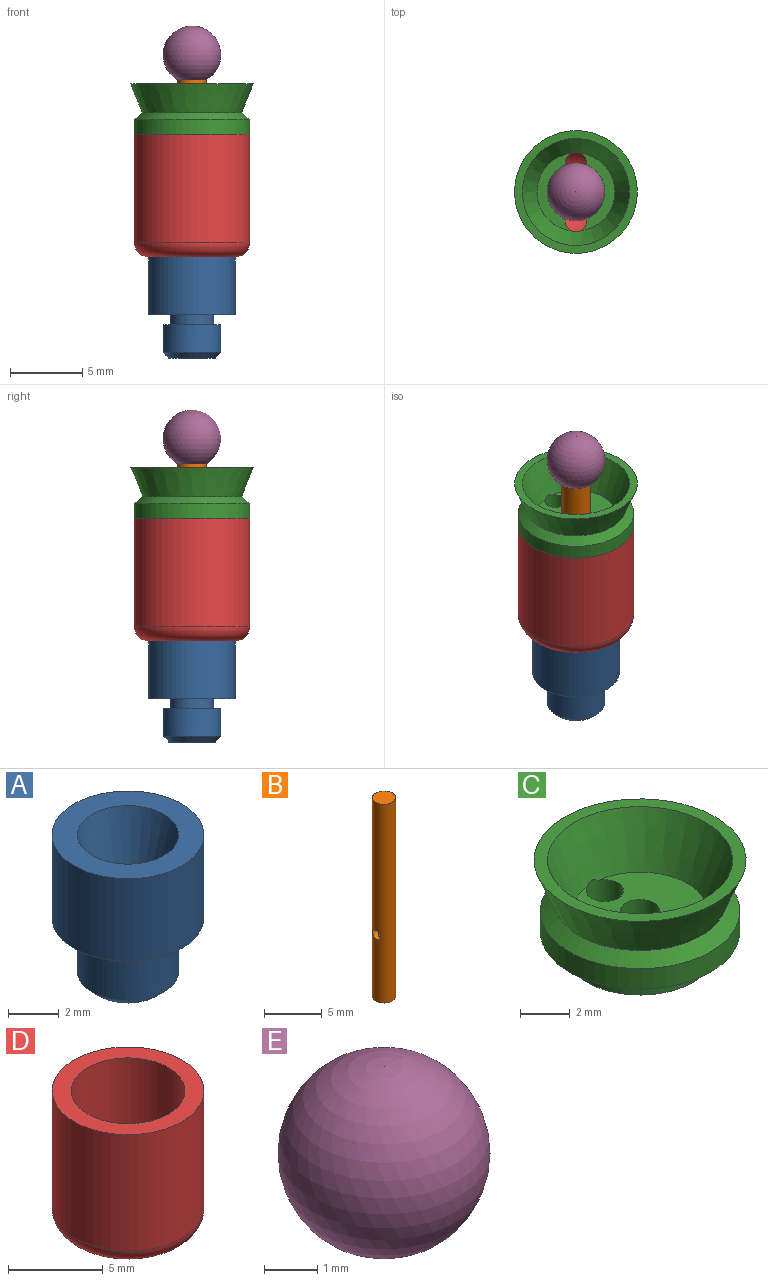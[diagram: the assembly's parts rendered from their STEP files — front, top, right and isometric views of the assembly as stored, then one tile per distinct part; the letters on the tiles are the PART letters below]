
ASSEMBLY  parts=5 mates=4
PART A: 11 faces, bbox 6x6x7 mm
  f0: plane 2x2mm, normal (0,0,1), area 1.1mm2, adj f8,f10
  f1: plane 3.2x3.2mm, normal (0,0,-1), area 6mm2, adj f9,f10
  f2: cylinder r=2mm len=4mm, axis (0,0,-1), area 23.9mm2, adj f3,f9
  f3: plane 4x4mm, normal (0,0,1), area 5.5mm2, adj f2,f4
  f4: cylinder r=1.5mm len=3mm, axis (0,0,-1), area 6.6mm2, adj f3,f5
  f5: plane 6x6mm, normal (0,0,-1), area 21.2mm2, adj f4,f6
  f6: cylinder r=3mm len=6mm, axis (0,0,-1), area 75.4mm2, adj f5,f7
  f7: plane 6x6mm, normal (0,0,1), area 15.7mm2, adj f6,f8
  f8: cone r=1mm half-angle=15.9deg, axis (0,0,1), area 34.3mm2, adj f0,f7
  f9: cone r=1.6mm half-angle=45deg, axis (0,0,1), area 6.4mm2, adj f1,f2
  f10: cylinder r=0.8mm len=3.5mm, axis (0,0,-1), area 17.6mm2, adj f0,f1
PART B: 8 faces, bbox 2x2x21 mm
  f0: cylinder r=1mm len=21mm, axis (0,0,-1), area 130.3mm2, adj f2,f3,f4,f7
  f1: cylinder r=0.5mm len=7mm, axis (0,0,-1), area 21mm2, adj f3,f4,f7
  f2: plane 2x2mm, normal (0,0,1), area 3.1mm2, adj f0
  f3: plane 2x2mm, normal (0,0,-1), area 2.4mm2, adj f0,f1
  f4: cylinder r=0.5mm len=1mm, axis (1,0,0), area 1.9mm2, adj f0,f1,f6
  f5: cone r=0mm half-angle=59deg, axis (0,0,-1), area 0.9mm2, adj f6
  f6: cylinder r=0.5mm len=1mm, axis (0,0,-1), area 2.1mm2, adj f4,f5,f7
  f7: cylinder r=0.5mm len=1mm, axis (1,0,0), area 1.9mm2, adj f0,f1,f6
PART C: 12 faces, bbox 8.5x8.5x4.5 mm
  f0: cone r=3.71mm half-angle=22deg, axis (0,0,1), area 54.2mm2, adj f7,f8,f10,f11
  f1: plane 6x6mm, normal (0,0,-1), area 22.7mm2, adj f2,f9,f10,f11
  f2: cylinder r=3mm len=6mm, axis (0,0,1), area 18.8mm2, adj f1,f3
  f3: plane 8x8mm, normal (0,0,-1), area 22mm2, adj f2,f4
  f4: cylinder r=4mm len=8mm, axis (0,0,1), area 25.1mm2, adj f3,f5
  f5: cone r=4mm half-angle=48.1deg, axis (0,0,-1), area 17.5mm2, adj f4,f6
  f6: cone r=3.44mm half-angle=22deg, axis (0,0,1), area 52.1mm2, adj f5,f7
  f7: plane 8.5x8.5mm, normal (0,0,1), area 13.5mm2, adj f0,f6
  f8: plane 5.4x5.37mm, normal (0,0,1), area 17.4mm2, adj f0,f9,f10,f11
  f9: cylinder r=0.8mm len=2mm, axis (0,0,-1), area 10.1mm2, adj f1,f8
  f10: cylinder r=0.75mm len=2.12mm, axis (0,0,-1), area 9.5mm2, adj f0,f1,f8
  f11: cylinder r=0.75mm len=2.12mm, axis (0,0,-1), area 9.5mm2, adj f0,f1,f8
PART D: 7 faces, bbox 8.7x8.7x8.5 mm
  f0: plane 8x8mm, normal (0,0,1), area 22mm2, adj f1,f5
  f1: cylinder r=3mm len=6mm, axis (0,0,1), area 103.7mm2, adj f0,f2
  f2: torus R=1mm, axis (0,0,1), area 44.9mm2, adj f1,f6
  f3: plane 6x6mm, normal (0,0,-1), area 25.1mm2, adj f4,f6
  f4: torus R=3mm, axis (0,0,1), area 35.9mm2, adj f3,f5
  f5: cylinder r=4mm len=8mm, axis (0,0,1), area 188.5mm2, adj f0,f4
  f6: cylinder r=1mm len=2mm, axis (0,0,-1), area 6.3mm2, adj f2,f3
PART E: 3 faces, bbox 4x4x3.7 mm
  f0: sphere r=2mm, area 46.9mm2, adj f2
  f1: cone r=0mm half-angle=59deg, axis (0,0,-1), area 3.7mm2, adj f2
  f2: cylinder r=1mm len=2.73mm, axis (0,0,-1), area 17.2mm2, adj f0,f1
PLACE A t=(0,0,3.5)mm
PLACE B t=(0,0,1)mm
PLACE C t=(0,0,14.5)mm
PLACE D t=(0,0,7)mm
PLACE E t=(0,0,19)mm
MATE fastened E.f1 <-> B.f0  axis (0,0,-1) through (0,0,22)mm
MATE fastened B.f0 <-> A.f2  axis (0,0,-1) through (0,0,1)mm
MATE fastened D.f1 <-> A.f2  axis (0,0,-1) through (0,0,7)mm
MATE fastened D.f1 <-> C.f0  axis (0,0,1) through (0,0,15.5)mm
